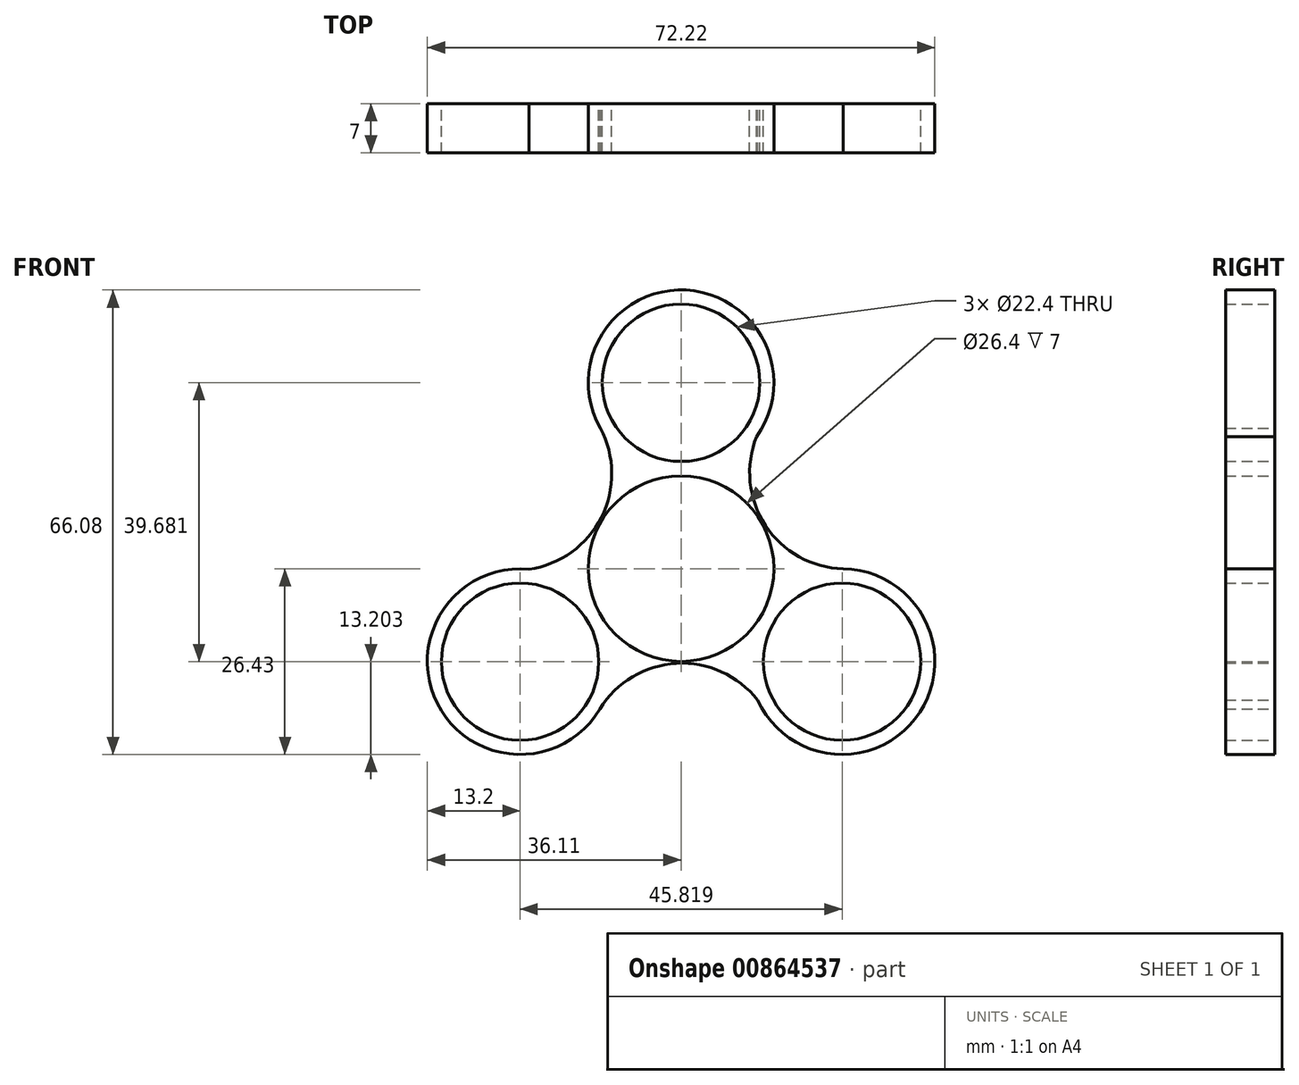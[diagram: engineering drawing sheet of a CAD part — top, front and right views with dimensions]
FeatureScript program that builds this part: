
annotation { "Feature Type Name" : "Feature", "Feature Type Description" : "" }
export const myFeature = defineFeature(function(context is Context, id is Id, definition is map)
    precondition{}
    {
        {
            var Q0;
            Q0=qCreatedBy(makeId("Front.planeOp"),FACE);
            var sketch = newSketch(context, id + "F0", { "sketchPlane" : qUnion([Q0])});
            skCircle(sketch, "E0", {"center": v(0, 0) * mm, "radius": 11.2 * mm});
            skCircle(sketch, "E1", {"center": v(0, 0) * mm, "radius": 13.2 * mm});
            skCircle(sketch, "E2", {"center": v(0, 26.45) * mm, "radius": 11.2 * mm});
            skArc(sketch, "E3", {"start": v(10.74, 18.78) * mm, "mid": v(0.71, 39.63) * mm, "end": v(-11.5, 19.99) * mm});
            skArc(sketch, "E4.1.0", {"start": v(-21.64, -0.09) * mm, "mid": v(-34.68, -19.2) * mm, "end": v(-11.55, -19.96) * mm});
            skArc(sketch, "E4.2.0", {"start": v(10.9, -18.7) * mm, "mid": v(33.97, -20.44) * mm, "end": v(23.06, -0.03) * mm});
            skCircle(sketch, "E5.1.0", {"center": v(-22.9, -13.23) * mm, "radius": 11.2 * mm});
            skCircle(sketch, "E5.2.0", {"center": v(22.9, -13.23) * mm, "radius": 11.2 * mm});
            skArc(sketch, "E6", {"start": v(10.74, 18.78) * mm, "mid": v(12.06, 6.06) * mm, "end": v(23.3, -0.03) * mm});
            skArc(sketch, "E7.1.0", {"start": v(-21.64, -0.09) * mm, "mid": v(-11.28, 7.42) * mm, "end": v(-11.62, 20.2) * mm});
            skArc(sketch, "E7.2.0", {"start": v(10.9, -18.7) * mm, "mid": v(-0.78, -13.48) * mm, "end": v(-11.68, -20.16) * mm});
            skSolve(sketch);
        }
        {
            var Q0;
            Q0 = qSketchRegion(id + "F0", true);
            extrude(context, id + "F1", {"entities" : qUnion([Q0]), "depth" : 7 * mm, "offsetDistance" : 25 * mm});
        }
    });
